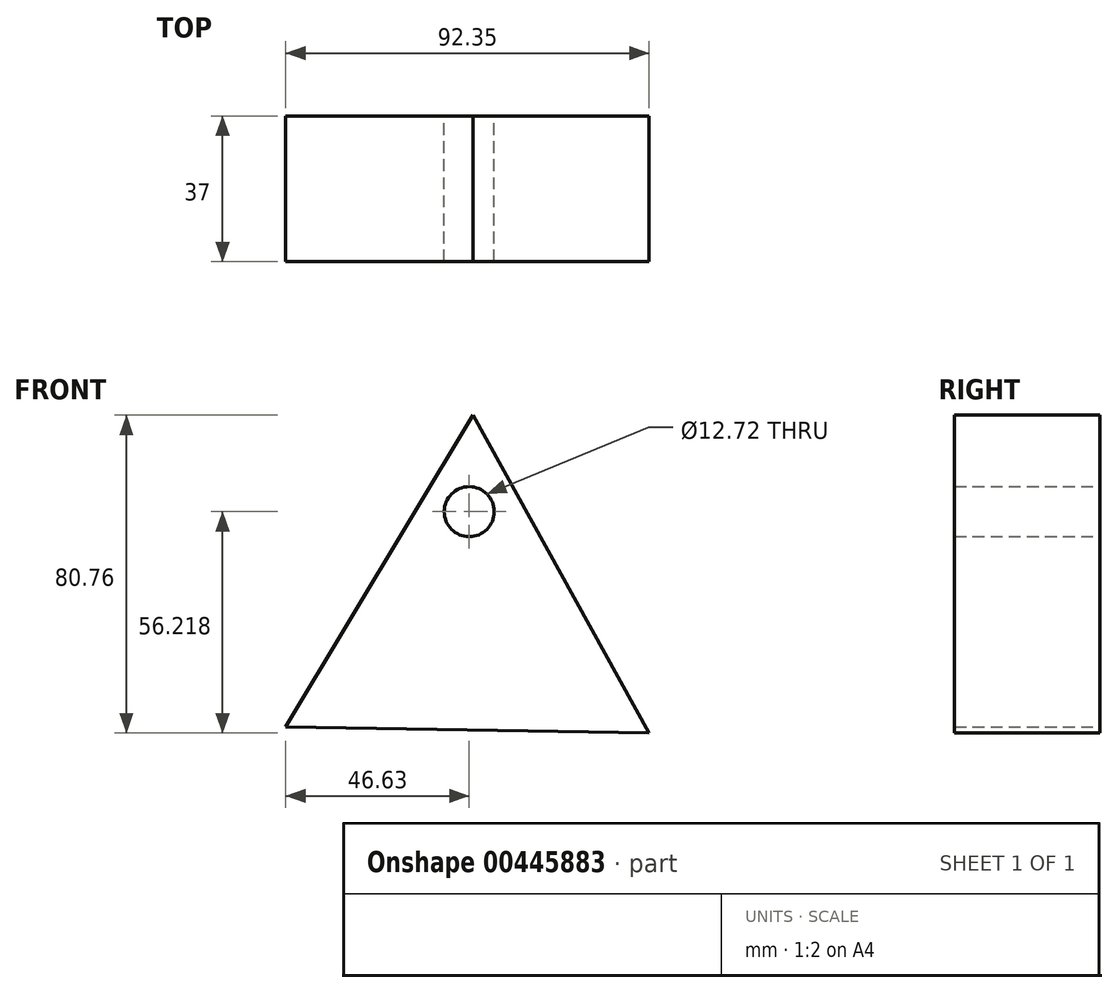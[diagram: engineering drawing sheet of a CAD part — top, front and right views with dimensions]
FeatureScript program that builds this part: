
annotation { "Feature Type Name" : "Feature", "Feature Type Description" : "" }
export const myFeature = defineFeature(function(context is Context, id is Id, definition is map)
    precondition{}
    {
        {
            var Q0;
            Q0=qCreatedBy(makeId("Front.planeOp"),FACE);
            var sketch = newSketch(context, id + "F0", { "sketchPlane" : qUnion([Q0])});
            skCircle(sketch, "E0.cCircle", {"center": v(0, 0) * mm, "radius": 26.66 * mm, "construction": true});
            skLineSegment(sketch, "E0.0", {"start": v(0.9, 53.32) * mm, "end": v(45.72, -27.44) * mm});
            skLineSegment(sketch, "E0.1", {"start": v(45.72, -27.44) * mm, "end": v(-46.63, -25.88) * mm});
            skLineSegment(sketch, "E0.2", {"start": v(-46.63, -25.88) * mm, "end": v(0.9, 53.32) * mm});
            skPoint(sketch, "E0.0.midPoint", {"position": v(23.31, 12.94) * mm});
            skCircle(sketch, "E1", {"center": v(0, 28.78) * mm, "radius": 6.36 * mm});
            skSolve(sketch);
        }
        {
            var Q0;
            Q0 = qSketchRegion(id + "F0", true);
            extrude(context, id + "F1", {"entities" : qUnion([Q0]), "depth" : 37 * mm});
        }
    });
